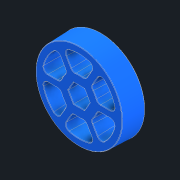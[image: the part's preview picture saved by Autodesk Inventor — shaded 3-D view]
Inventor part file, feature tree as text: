
AUTODESK INVENTOR PART (.ipt)
format: ipt  version: 2021 (Build 250183000, 183)  size: 778,752 bytes
history: native  units: in
note: dims shown in document units (in); Inventor stores cm internally (conversion verified against a paired STEP export)
features: fillet x1
ambient origin geometry x8: Origin, YZ Plane, XZ Plane, XY Plane, X Axis, Y Axis, Z Axis, Center Point
bodies: Solid1 (feature_tree)
feature tree (1):
  fillet  "Fillet3"  [1 undecoded]
note: 1 required parameter value undecoded (feature->parameter linkage not recoverable at this tier; creation-order binding heuristic only, values carry confidence <= 0.55)
